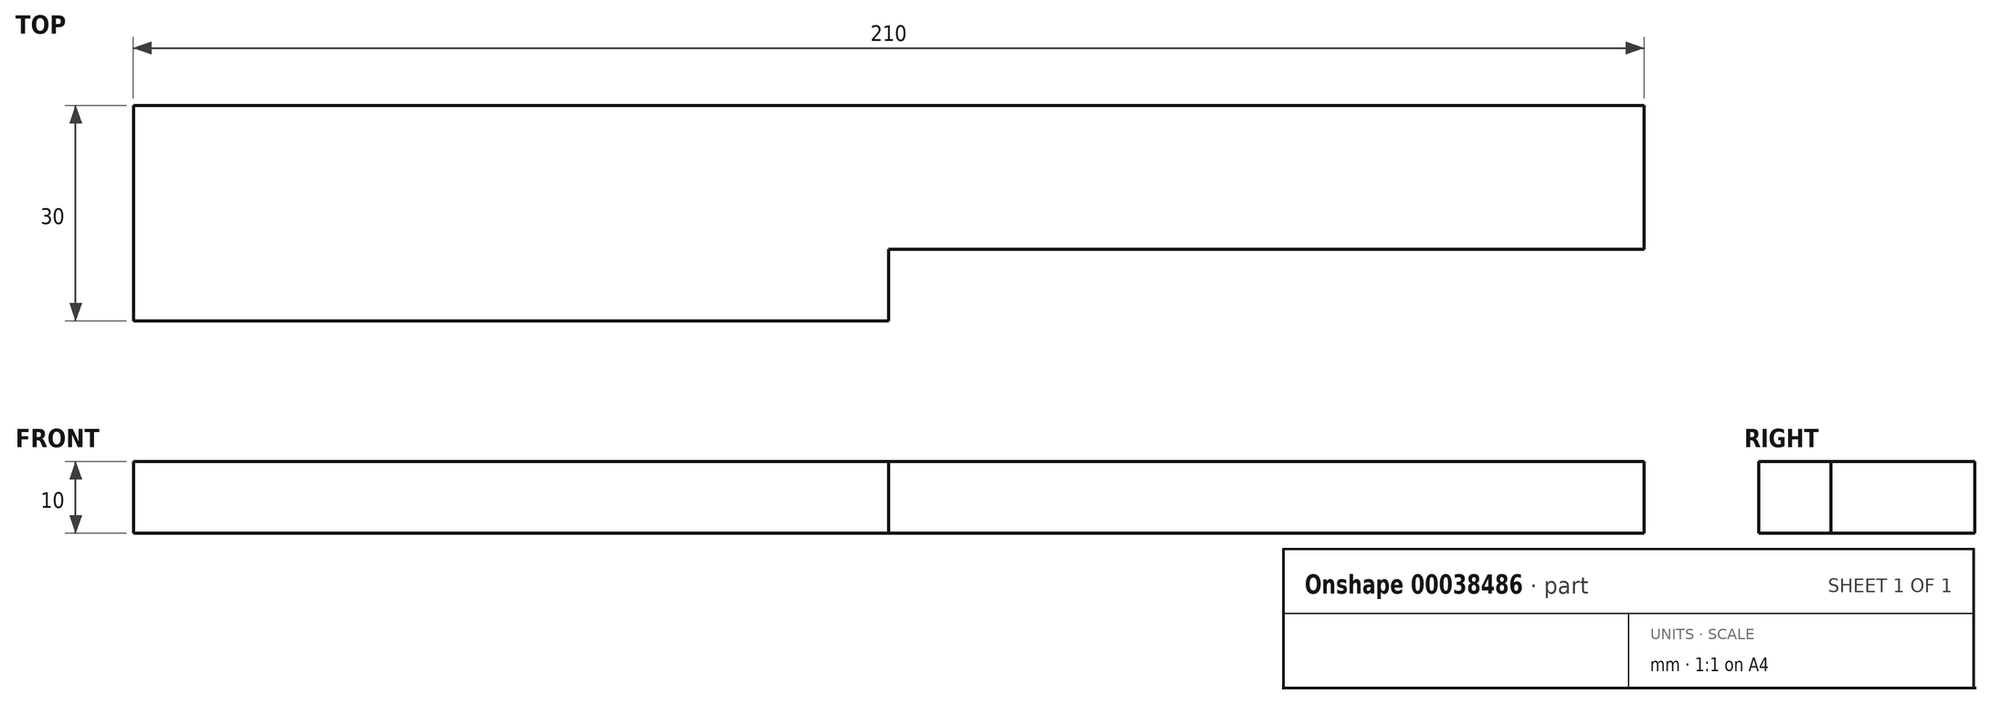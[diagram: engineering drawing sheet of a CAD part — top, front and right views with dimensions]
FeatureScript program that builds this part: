
annotation { "Feature Type Name" : "Feature", "Feature Type Description" : "" }
export const myFeature = defineFeature(function(context is Context, id is Id, definition is map)
    precondition{}
    {
        {
            var Q0;
            Q0=qCreatedBy(makeId("Top.planeOp"),FACE);
            var sketch = newSketch(context, id + "F0", { "sketchPlane" : qUnion([Q0])});
            skLineSegment(sketch, "E0.bottom", {"start": v(-115.38, 30) * mm, "end": v(-10.38, 30) * mm});
            skLineSegment(sketch, "E0.top", {"start": v(-115.38, 0) * mm, "end": v(-10.38, 0) * mm});
            skLineSegment(sketch, "E0.left", {"start": v(-115.38, 30) * mm, "end": v(-115.38, 0) * mm});
            skLineSegment(sketch, "E0.right", {"start": v(-10.38, 30) * mm, "end": v(-10.38, 0) * mm});
            skLineSegment(sketch, "E1.bottom", {"start": v(-10.38, 30) * mm, "end": v(94.62, 30) * mm});
            skLineSegment(sketch, "E1.top", {"start": v(-10.38, 10) * mm, "end": v(94.62, 10) * mm});
            skLineSegment(sketch, "E1.left", {"start": v(-10.38, 30) * mm, "end": v(-10.38, 10) * mm});
            skLineSegment(sketch, "E1.right", {"start": v(94.62, 30) * mm, "end": v(94.62, 10) * mm});
            skLineSegment(sketch, "E2.top", {"start": v(-10.38, 0) * mm, "end": v(94.62, 0) * mm});
            skLineSegment(sketch, "E2.left", {"start": v(-10.38, 10) * mm, "end": v(-10.38, 0) * mm});
            skLineSegment(sketch, "E2.right", {"start": v(94.62, 10) * mm, "end": v(94.62, 0) * mm});
            skSolve(sketch);
        }
        {
            var Q0;
            Q0=makeQuery(id+"F0.imprint","IMPRINT",FACE,{"disambiguationData":[TD([[makeQuery(id+"F0.imprint","IMPRINT",EDGE,{"derivedFrom":sQuery(id+"F0.wireOp",EDGE,"E1.top")}),-1.0]])]});
            var Q1;
            Q1=makeQuery(id+"F0.imprint","IMPRINT",FACE,{"disambiguationData":[TD([[makeQuery(id+"F0.imprint","IMPRINT",EDGE,{"derivedFrom":sQuery(id+"F0.wireOp",EDGE,"E1.bottom")}),-1.0]])]});
            var Q2;
            Q2=makeQuery(id+"F0.imprint","IMPRINT",FACE,{"disambiguationData":[TD([[makeQuery(id+"F0.imprint","IMPRINT",EDGE,{"derivedFrom":sQuery(id+"F0.wireOp",EDGE,"E0.bottom")}),-1.0]])]});
            extrude(context, id + "F1", {"entities" : qUnion([Q0, Q1, Q2]), "depth" : 10 * mm});
        }
    });
